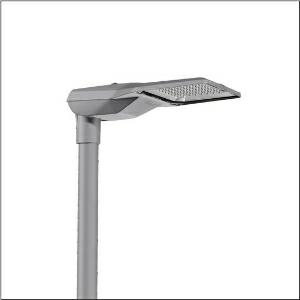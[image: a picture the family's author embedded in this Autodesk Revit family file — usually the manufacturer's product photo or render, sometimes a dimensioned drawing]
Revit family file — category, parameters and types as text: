
# Revit family: streetlight_sl_21_midi___st1_0ab_5xe3m33s08lb_591c
name_source: partatom
category: Lighting Fixtures
units: mm (PartAtom-declared; Revit-internal decimal feet)

## family parameters
Cut with Voids When Loaded = No
Host = Face
Light Source = No
Part Type = Normal
Room Calculation Point = No
Round Connector Dimension = Use Diameter
Shared = No

## types (1)
- --- (1 x LED, 12620 lm, 99.6 W, 3000K)
    Apparent Load = 100 VA
    CIE Flux Codes = 38 73 97 100 100
    Color Rendering = 70
    Color Temperature = 3000K
    Default Elevation = 1800 mm
    Description = Streetlight SL 21 midi, mast luminaire, primary light control with lens, of PMMA, primary optical cover: cover, of toughened safety glass, transparent, light distribution: ST1.0aB, light emission: direct distribution, primary light characteristic: asymmetric, installation type: side-entry, post-top, LED, High Power LED, rated luminous flux: 12.620lm, luminous efficacy: 127lm/W, light colour: 730, colour temperature: 3000K, control gear: D4i, control: flexible luminous flux parameterisation, time-dependent luminous flux control, constant luminous flux control, overheat protection, pre-setting: logarithmic dimming characteristic, mains connection: 230..240V, AC, 50/60Hz, start of lifetime: 100W, end of service life: 102W, reduction: 46W, luminaire housing, of diecast aluminium, powder-coated, SITECO metallic grey (DB 702S), corrosivity category C5 high according to DIN EN ISO 12944, please order mast flange separately, inclination adjustable: 0°, 5°, 10°, 15°, sealing non-destructively replaceable, multi-level sealing system, length: 644mm, width: 335mm, height: 110mm, mast flange for spigot size: 42mm (side-entry): 5XC10008XM4, 60/48mm (side-entry/post-top): 5XC10108XM2, 76/60mm (side-entry/post-top): 5XC10108XM1, mounting height: 4..8m, Smart Interface above, protection rating (complete): IP66, insulation class (complete): insulation class II (safety insulation), certification: CE, ENEC, ENEC+, VDE, impact resistance: IK10, permissible operating ambient temperature for outdoor applications: -40..+50°C, standard-compliant lighting for roads and squares, packaging unit: 1 piece

Light Distribution: ST1.0aB
    Height = 111 mm
    Lamp = 1 x LED
    Lamp Light Flux = 12620 lm
    Lamp Power = 99.6 W
    Lamp count = 1
    Length = 644 mm
    Luminous efficacy = 127 lm/W
    Manufacturer = Siteco
    ModVariant = No
    Model = 5XE3M33S08LB
    Number of Poles = 1
    OnlyDefault = Yes
    Power Factor = 1
    Product Name = Streetlight SL 21 midi | ST1.0aB
    Product group = mast luminaire | pylon top
    ProductGroupID = 6100
    Protection Class = Protection class II
    Protection Degree = IP 66
    RLX_Detail_Level = 1
    RLX_Emergency_Light_Flux = 0 lm
    RLX_Emergency_Type = 0
    RLX_Emergency_Type_DB = No
    RlxData = <blob elided: 26813 chars, md5=27fea71e>
    Socket = socket
    Standby Power = 0 W
    System Light Flux = 12620 lm
    System Power = 100 W
    Type Comments = factory setting: luminous flux: 100 % | dim-lin: 254 | 1020 mA
    Type Image = l_1004302.jpg
    URL = http://relux.com
    VarID = @adj_030627
    Voltage = 0 V
    Weight = 0.00 kg
    Width = 336 mm

## geometry (parser evidence)
native form markers: Blend x4, Sweep x12
no freeform markers — native parametric forms only
